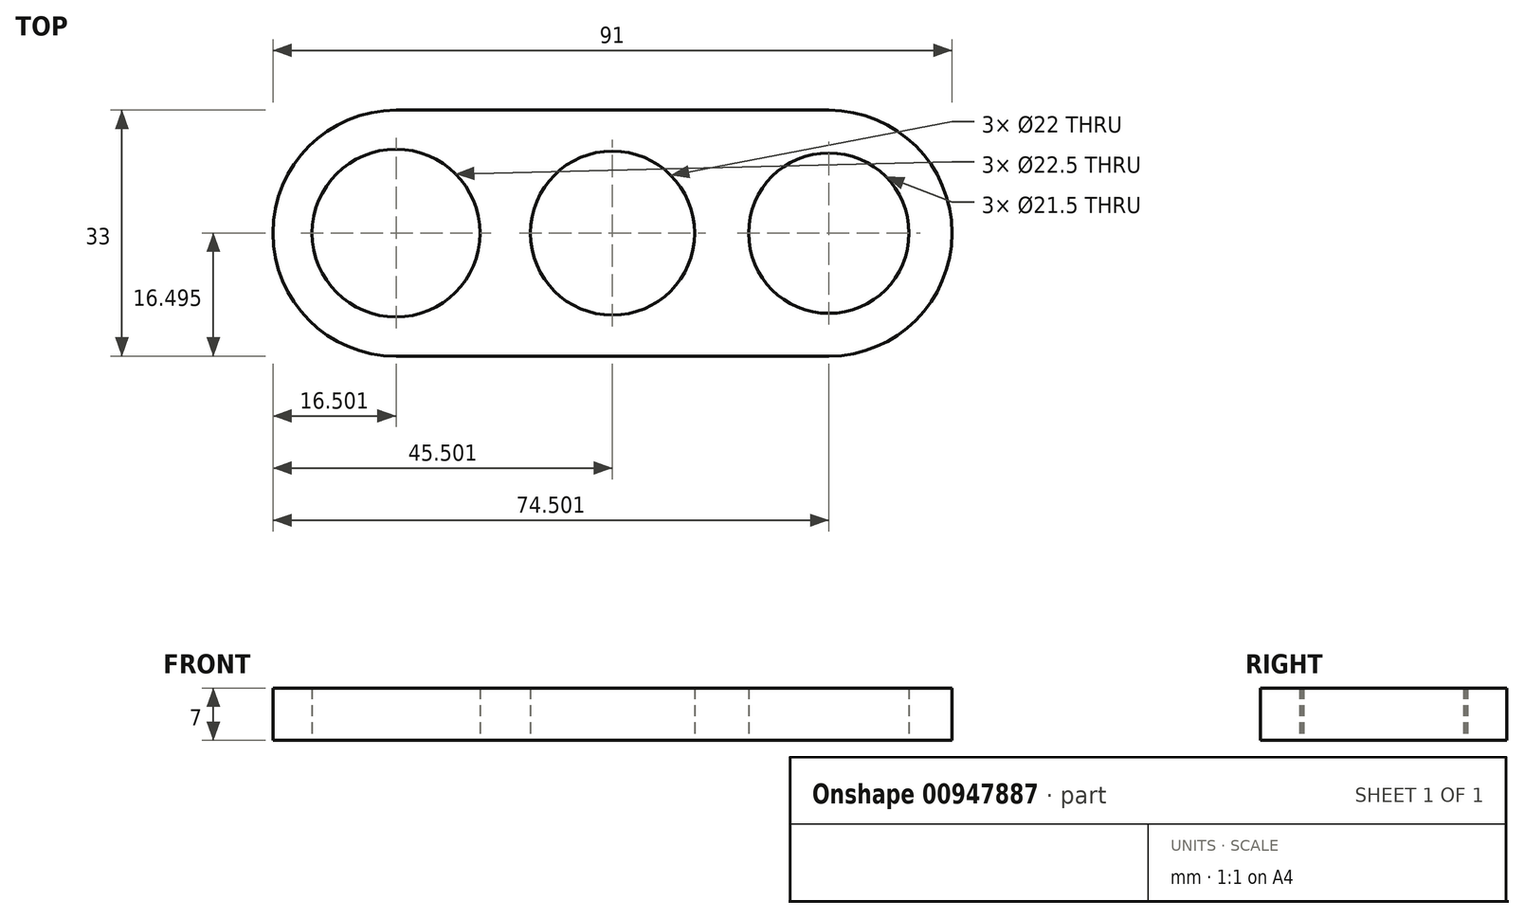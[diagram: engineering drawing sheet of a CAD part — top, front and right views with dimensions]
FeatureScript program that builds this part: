
annotation { "Feature Type Name" : "Feature", "Feature Type Description" : "" }
export const myFeature = defineFeature(function(context is Context, id is Id, definition is map)
    precondition{}
    {
        {
            var Q0;
            Q0=qCreatedBy(makeId("Top.planeOp"),FACE);
            var sketch = newSketch(context, id + "F0", { "sketchPlane" : qUnion([Q0])});
            skLineSegment(sketch, "E0", {"start": v(-32.79, 5.8) * mm, "end": v(25.21, 5.8) * mm, "construction": true});
            skCircle(sketch, "E1", {"center": v(-32.79, 5.8) * mm, "radius": 11.25 * mm});
            skCircle(sketch, "E2", {"center": v(-3.79, 5.8) * mm, "radius": 11 * mm});
            skCircle(sketch, "E3", {"center": v(25.21, 5.8) * mm, "radius": 10.75 * mm});
            skCircle(sketch, "E4", {"center": v(-32.79, 5.8) * mm, "radius": 16.5 * mm});
            skCircle(sketch, "E5", {"center": v(25.21, 5.8) * mm, "radius": 16.5 * mm});
            skLineSegment(sketch, "E6", {"start": v(-32.79, -10.7) * mm, "end": v(25.21, -10.7) * mm});
            skLineSegment(sketch, "E7", {"start": v(-32.79, 22.3) * mm, "end": v(25.21, 22.3) * mm});
            skSolve(sketch);
        }
        {
            var Q0;
            Q0=makeQuery(id+"F0.imprint","IMPRINT",FACE,{"disambiguationData":[TD([[makeQuery(id+"F0.imprint","IMPRINT",EDGE,{"derivedFrom":sQuery(id+"F0.wireOp",EDGE,"E1")}),-1.0]])]});
            var Q1;
            {var subQ5=sQuery(id+"F0.wireOp",EDGE,"E6");Q1=makeQuery(id+"F0.imprint","IMPRINT",FACE,{"disambiguationData":[TD([[makeQuery(id+"F0.imprint","IMPRINT",EDGE,{"derivedFrom":subQ5}),1.0]])]});}
            var Q2;
            {var subQ5=sQuery(id+"F0.wireOp",EDGE,"E7");Q2=makeQuery(id+"F0.imprint","IMPRINT",FACE,{"disambiguationData":[TD([[makeQuery(id+"F0.imprint","IMPRINT",EDGE,{"derivedFrom":subQ5}),-1.0]])]});}
            var Q3;
            Q3=makeQuery(id+"F0.imprint","IMPRINT",FACE,{"disambiguationData":[TD([[makeQuery(id+"F0.imprint","IMPRINT",EDGE,{"derivedFrom":sQuery(id+"F0.wireOp",EDGE,"E3")}),-1.0]])]});
            extrude(context, id + "F1", {"entities" : qUnion([Q0, Q1, Q2, Q3]), "depth" : 7 * mm, "offsetDistance" : 25 * mm});
        }
    });
